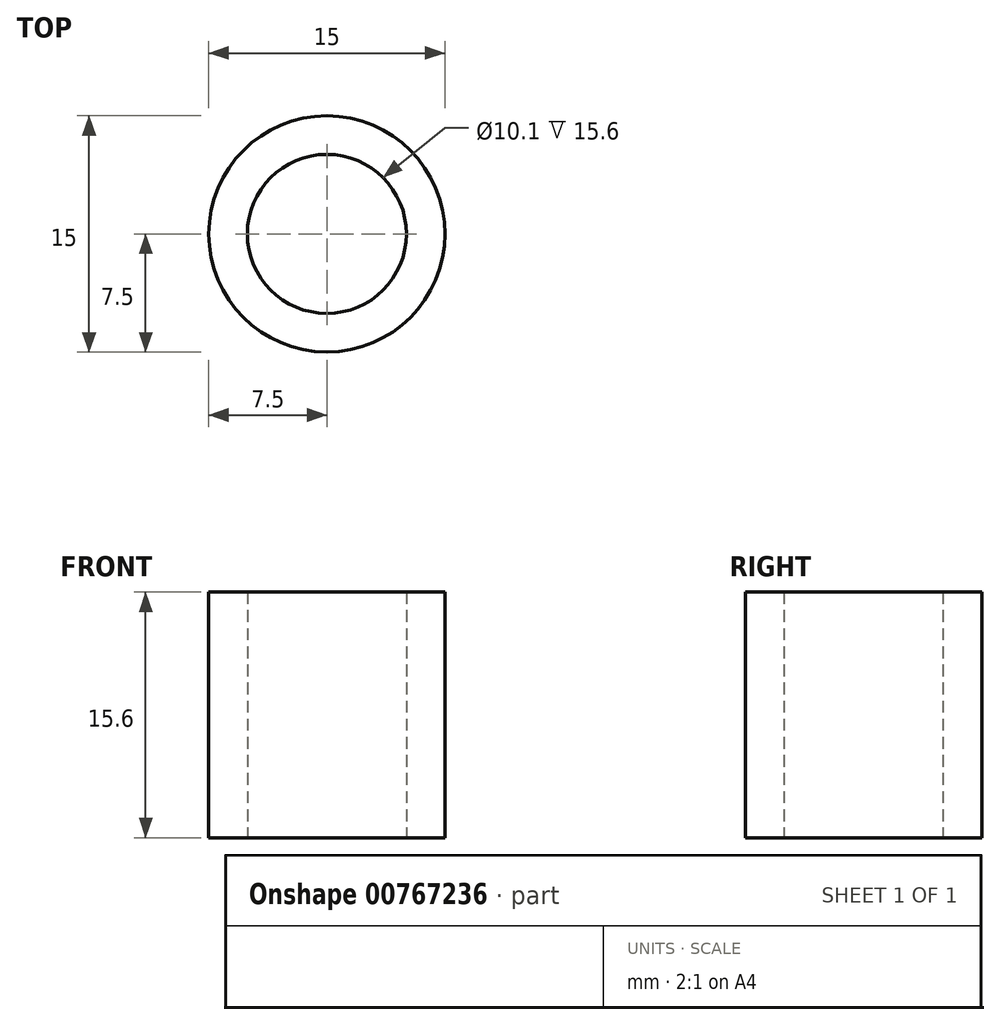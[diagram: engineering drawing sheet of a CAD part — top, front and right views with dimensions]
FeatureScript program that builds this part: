
annotation { "Feature Type Name" : "Feature", "Feature Type Description" : "" }
export const myFeature = defineFeature(function(context is Context, id is Id, definition is map)
    precondition{}
    {
        {
            var Q0;
            Q0=qCreatedBy(makeId("Top.planeOp"),FACE);
            var sketch = newSketch(context, id + "F0", { "sketchPlane" : qUnion([Q0])});
            skCircle(sketch, "E0", {"center": v(0, 0) * mm, "radius": 7.5 * mm});
            skCircle(sketch, "E1", {"center": v(0, 0) * mm, "radius": 13 * mm});
            skCircle(sketch, "E2", {"center": v(0, 0) * mm, "radius": 5.05 * mm});
            skSolve(sketch);
        }
        {
            var Q0;
            Q0=makeQuery(id+"F0.imprint","IMPRINT",FACE,{"disambiguationData":[TD([[makeQuery(id+"F0.imprint","IMPRINT",EDGE,{"derivedFrom":sQuery(id+"F0.wireOp",EDGE,"E0")}),1.0]])]});
            extrude(context, id + "F1", {"entities" : qUnion([Q0]), "depth" : 15.6 * mm, "offsetDistance" : 25 * mm});
        }
    });
